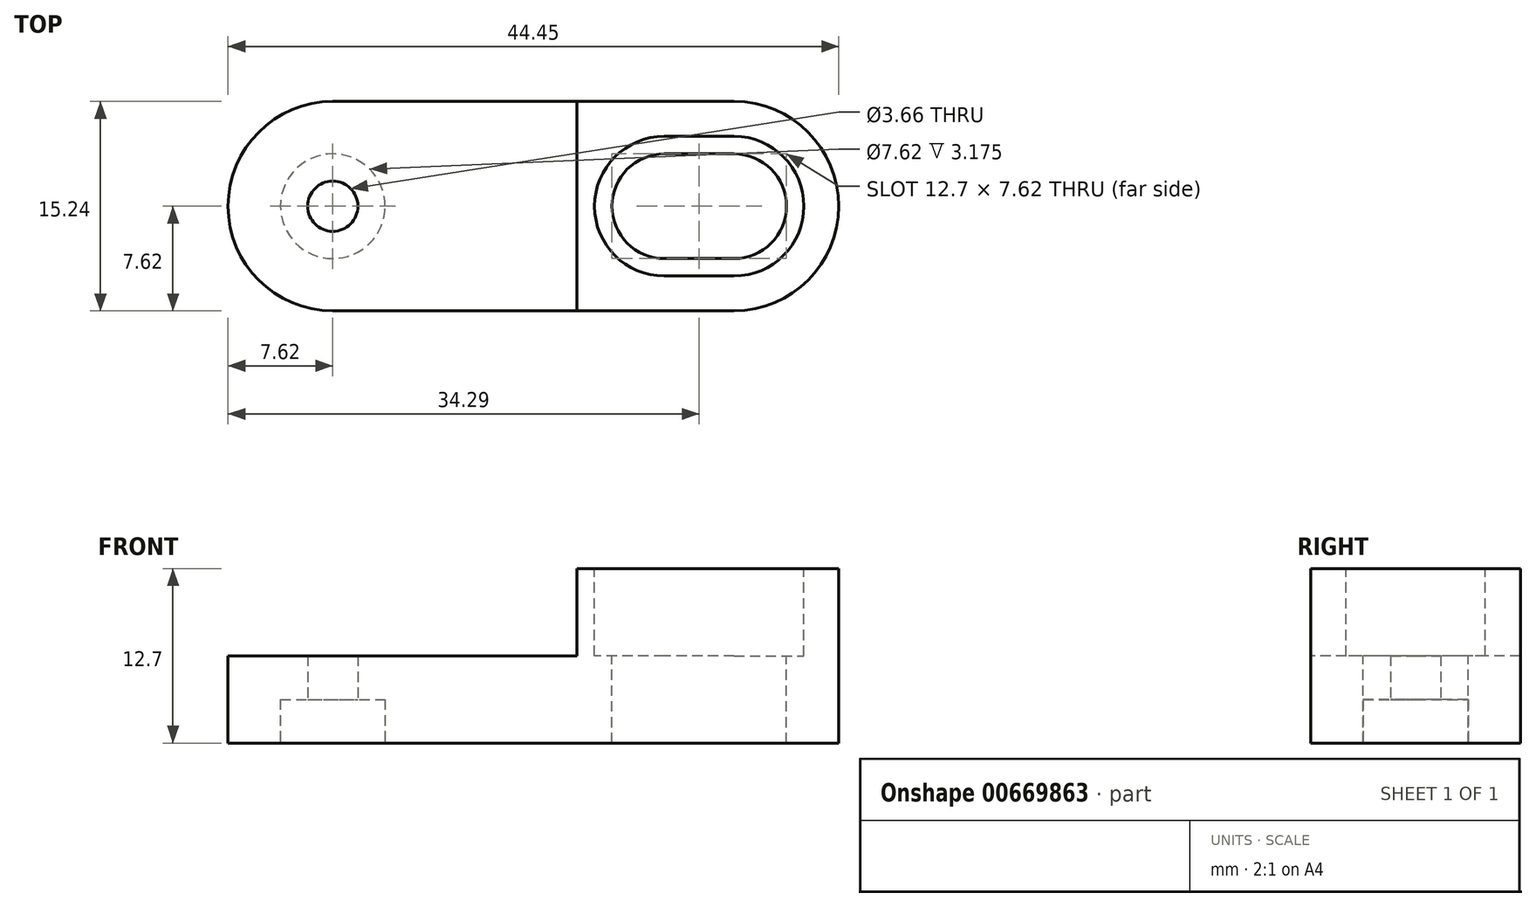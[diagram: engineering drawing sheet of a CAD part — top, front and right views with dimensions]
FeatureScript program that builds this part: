
annotation { "Feature Type Name" : "Feature", "Feature Type Description" : "" }
export const myFeature = defineFeature(function(context is Context, id is Id, definition is map)
    precondition{}
    {
        {
            var Q0;
            Q0=qCreatedBy(makeId("Top.planeOp"),FACE);
            var sketch = newSketch(context, id + "F0", { "sketchPlane" : qUnion([Q0])});
            skLineSegment(sketch, "E0.bottom", {"start": v(7.62, 0) * mm, "end": v(36.83, 0) * mm});
            skLineSegment(sketch, "E0.top", {"start": v(7.62, 15.24) * mm, "end": v(36.83, 15.24) * mm});
            skLineSegment(sketch, "E0.left", {"start": v(0, 7.62) * mm, "end": v(0, 7.62) * mm});
            skLineSegment(sketch, "E0.right", {"start": v(44.45, 7.62) * mm, "end": v(44.45, 7.62) * mm});
            skPoint(sketch, "E1.visualSharp", {"position": v(0, 15.24) * mm});
            skArc(sketch, "E1.filletArc", {"start": v(7.62, 15.24) * mm, "mid": v(2.23, 13) * mm, "end": v(0, 7.62) * mm});
            skPoint(sketch, "E2.visualSharp", {"position": v(0, 0) * mm});
            skArc(sketch, "E2.filletArc", {"start": v(0, 7.62) * mm, "mid": v(2.23, 2.23) * mm, "end": v(7.62, 0) * mm});
            skPoint(sketch, "E3.visualSharp", {"position": v(44.45, 15.24) * mm});
            skArc(sketch, "E3.filletArc", {"start": v(44.45, 7.62) * mm, "mid": v(42.22, 13) * mm, "end": v(36.83, 15.24) * mm});
            skPoint(sketch, "E4.visualSharp", {"position": v(44.45, 0) * mm});
            skArc(sketch, "E4.filletArc", {"start": v(36.83, 0) * mm, "mid": v(42.22, 2.23) * mm, "end": v(44.45, 7.62) * mm});
            skSolve(sketch);
        }
        {
            var Q0;
            Q0=qSketchRegion(id+"F0",true);
            extrude(context, id + "F1", {"entities" : qUnion([Q0]), "depth" : 6.35 * mm, "offsetDistance" : 25.4 * mm});
        }
        {
            var Q0;
            Q0=makeQuery(id+"F1.opExtrude","CAP_FACE",FACE,{"disambiguationData":[OSD([sQuery(id+"F0.wireOp",EDGE,"E0.bottom"),sQuery(id+"F0.wireOp",EDGE,"E0.top"),sQuery(id+"F0.wireOp",EDGE,"E1.filletArc"),sQuery(id+"F0.wireOp",EDGE,"E2.filletArc"),sQuery(id+"F0.wireOp",EDGE,"E3.filletArc"),sQuery(id+"F0.wireOp",EDGE,"E4.filletArc")])],"isStart":false});
            var sketch = newSketch(context, id + "F2", { "sketchPlane" : qUnion([Q0])});
            skPoint(sketch, "E5", {"position": v(7.62, 7.62) * mm});
            skSolve(sketch);
        }
        {
            var Q0;
            Q0=sQuery(id+"F2.wireOp",VERTEX,"E5");
            var Q1;
            Q1=makeQuery(id+"F1.opExtrude","SWEPT_BODY",BODY,{"disambiguationData":[OSD([sQuery(id+"F0.wireOp",EDGE,"E0.bottom"),sQuery(id+"F0.wireOp",EDGE,"E0.top"),sQuery(id+"F0.wireOp",EDGE,"E1.filletArc"),sQuery(id+"F0.wireOp",EDGE,"E2.filletArc"),sQuery(id+"F0.wireOp",EDGE,"E3.filletArc"),sQuery(id+"F0.wireOp",EDGE,"E4.filletArc")])]});
            hole(context, id + "F3", {"style" : HoleStyle.SIMPLE, "endStyle" : HoleEndStyle.THROUGH, "standardTappedOrClearance" : lookupTablePath({ "standard" : "ANSI", "fit" : "Close", "size" : "#6", "type" : "Clearance" }), "standardBlindInLast" : lookupTablePath({ "fit" : "Close", "standard" : "ANSI", "size" : "#6", "type" : "Clearance" }), "holeDiameter" : 3.66 * mm, "majorDiameter" : 6.35 * mm, "isTappedThrough" : true, "tappedDepth" : 2.4 * mm, "tapClearance" : 3, "startFromSketch" : true, "locations" : qUnion([Q0]), "scope" : qUnion([Q1])});
        }
        {
            var Q0;
            Q0=makeQuery(id+"F1.opExtrude","CAP_FACE",FACE,{"disambiguationData":[OSD([sQuery(id+"F0.wireOp",EDGE,"E0.bottom"),sQuery(id+"F0.wireOp",EDGE,"E0.top"),sQuery(id+"F0.wireOp",EDGE,"E1.filletArc"),sQuery(id+"F0.wireOp",EDGE,"E2.filletArc"),sQuery(id+"F0.wireOp",EDGE,"E3.filletArc"),sQuery(id+"F0.wireOp",EDGE,"E4.filletArc")])],"isStart":false});
            var sketch = newSketch(context, id + "F4", { "sketchPlane" : qUnion([Q0])});
            skLineSegment(sketch, "E6", {"start": v(25.4, 15.24) * mm, "end": v(25.4, 0) * mm});
            skLineSegment(sketch, "E7", {"start": v(25.4, 15.24) * mm, "end": v(36.83, 15.24) * mm});
            skLineSegment(sketch, "E8", {"start": v(25.4, 0) * mm, "end": v(36.83, 0) * mm});
            skArc(sketch, "E9.0", {"start": v(36.83, 0) * mm, "mid": v(44.45, 7.62) * mm, "end": v(36.83, 15.24) * mm});
            skSolve(sketch);
        }
        {
            var Q0;
            Q0=qSketchRegion(id+"F4",true);
            extrude(context, id + "F5", {"entities" : qUnion([Q0]), "operationType" : NewBodyOperationType.ADD, "depth" : 6.35 * mm, "offsetDistance" : 25.4 * mm});
        }
        {
            var Q0;
            Q0=makeQuery(id+"F5.opExtrude","CAP_FACE",FACE,{"disambiguationData":[OSD([sQuery(id+"F4.wireOp",EDGE,"E6"),sQuery(id+"F4.wireOp",EDGE,"E7"),sQuery(id+"F4.wireOp",EDGE,"E8"),sQuery(id+"F4.wireOp",EDGE,"E9.0")])],"isStart":false});
            var sketch = newSketch(context, id + "F6", { "sketchPlane" : qUnion([Q0])});
            skLineSegment(sketch, "E10", {"start": v(31.75, 7.62) * mm, "end": v(36.83, 7.62) * mm});
            skArc(sketch, "E11.0.startCap", {"start": v(31.75, 3.81) * mm, "mid": v(27.94, 7.62) * mm, "end": v(31.75, 11.43) * mm});
            skArc(sketch, "E11.0.endCap", {"start": v(36.83, 11.43) * mm, "mid": v(40.64, 7.62) * mm, "end": v(36.83, 3.81) * mm});
            skLineSegment(sketch, "E11.0.left", {"start": v(31.75, 11.43) * mm, "end": v(36.83, 11.43) * mm});
            skLineSegment(sketch, "E11.0.right", {"start": v(31.75, 3.81) * mm, "end": v(36.83, 3.81) * mm});
            skSolve(sketch);
        }
        {
            var Q0;
            Q0=qSketchRegion(id+"F6",true);
            extrude(context, id + "F7", {"entities" : qUnion([Q0]), "operationType" : NewBodyOperationType.REMOVE, "endBound" : BoundingType.THROUGH_ALL, "oppositeDirection" : true, "depth" : 25.4 * mm, "offsetDistance" : 25.4 * mm});
        }
        {
            var Q0;
            Q0=makeQuery(id+"F5.opExtrude","CAP_FACE",FACE,{"disambiguationData":[OSD([sQuery(id+"F4.wireOp",EDGE,"E6"),sQuery(id+"F4.wireOp",EDGE,"E7"),sQuery(id+"F4.wireOp",EDGE,"E8"),sQuery(id+"F4.wireOp",EDGE,"E9.0")])],"isStart":false});
            var sketch = newSketch(context, id + "F8", { "sketchPlane" : qUnion([Q0])});
            skLineSegment(sketch, "E12", {"start": v(31.75, 7.62) * mm, "end": v(36.83, 7.62) * mm});
            skArc(sketch, "E13.0.startCap", {"start": v(31.75, 2.54) * mm, "mid": v(26.67, 7.62) * mm, "end": v(31.75, 12.7) * mm});
            skArc(sketch, "E13.0.endCap", {"start": v(36.83, 12.7) * mm, "mid": v(41.91, 7.62) * mm, "end": v(36.83, 2.54) * mm});
            skLineSegment(sketch, "E13.0.left", {"start": v(31.75, 12.7) * mm, "end": v(36.83, 12.7) * mm});
            skLineSegment(sketch, "E13.0.right", {"start": v(31.75, 2.54) * mm, "end": v(36.83, 2.54) * mm});
            skSolve(sketch);
        }
        {
            var Q0;
            Q0=qSketchRegion(id+"F8",true);
            extrude(context, id + "F9", {"entities" : qUnion([Q0]), "operationType" : NewBodyOperationType.REMOVE, "oppositeDirection" : true, "depth" : 6.35 * mm, "offsetDistance" : 25.4 * mm});
        }
        {
            var Q0;
            Q0=makeQuery(id+"F1.opExtrude","CAP_FACE",FACE,{"disambiguationData":[OSD([sQuery(id+"F0.wireOp",EDGE,"E0.bottom"),sQuery(id+"F0.wireOp",EDGE,"E0.top"),sQuery(id+"F0.wireOp",EDGE,"E1.filletArc"),sQuery(id+"F0.wireOp",EDGE,"E2.filletArc"),sQuery(id+"F0.wireOp",EDGE,"E3.filletArc"),sQuery(id+"F0.wireOp",EDGE,"E4.filletArc")])],"isStart":true});
            var sketch = newSketch(context, id + "F10", { "sketchPlane" : qUnion([Q0])});
            skCircle(sketch, "E14", {"center": v(7.62, -7.62) * mm, "radius": 3.8 * mm});
            skSolve(sketch);
        }
        {
            var Q0;
            Q0=qSketchRegion(id+"F10",true);
            extrude(context, id + "F11", {"entities" : qUnion([Q0]), "operationType" : NewBodyOperationType.REMOVE, "oppositeDirection" : true, "depth" : 3.17 * mm, "offsetDistance" : 25.4 * mm});
        }
    });
